SOLIDWORKS PART (.sldprt)
format: sldprt  version: not decoded by parser v0  size: 279,040 bytes
history: native  units: mm
features: sketch x4, extrude x4, fillet x4, plane x3, material x1 (+9 scaffold rows collapsed)
feature tree (25):
  scaffold x9  (default folders/planes/origin — collapsed)
  material  "Material <not specified>"
  plane  "Face"
  plane  "Dessus"
  plane  "Droite"
  sketch  "Esquisse1"  dims[c1.D2=0.5mm c1.D1=3.6mm c2.D2=3.6mm]
  extrude  "Extrusion1"  Depth=1.8mm
  fillet  "Congé1"  Radius=0.7mm
  sketch  "Esquisse3"  dims[D1=0.8mm D2=0.8mm D3=0.8mm]
  extrude  "Extrusion3"  Depth=2mm
  sketch  "Esquisse4"  dims[D1=0.8mm D2=0.8mm]
  extrude  "Extrusion4"  Depth=2mm
  sketch  "Esquisse5"  dims[D1=0.8mm D2=6.5mm]
  extrude  "Extrusion5"  Depth=0.8mm
  fillet  "Congé2"  Radius=0.4mm
  fillet  "Congé3"  Radius=0.35mm
  fillet  "Congé5"  Radius=0.3mm
decode coverage: 12 of 12 modeling features carry decoded parameters
note: suppression state not decoded; provenance and decode notes live in map.json
